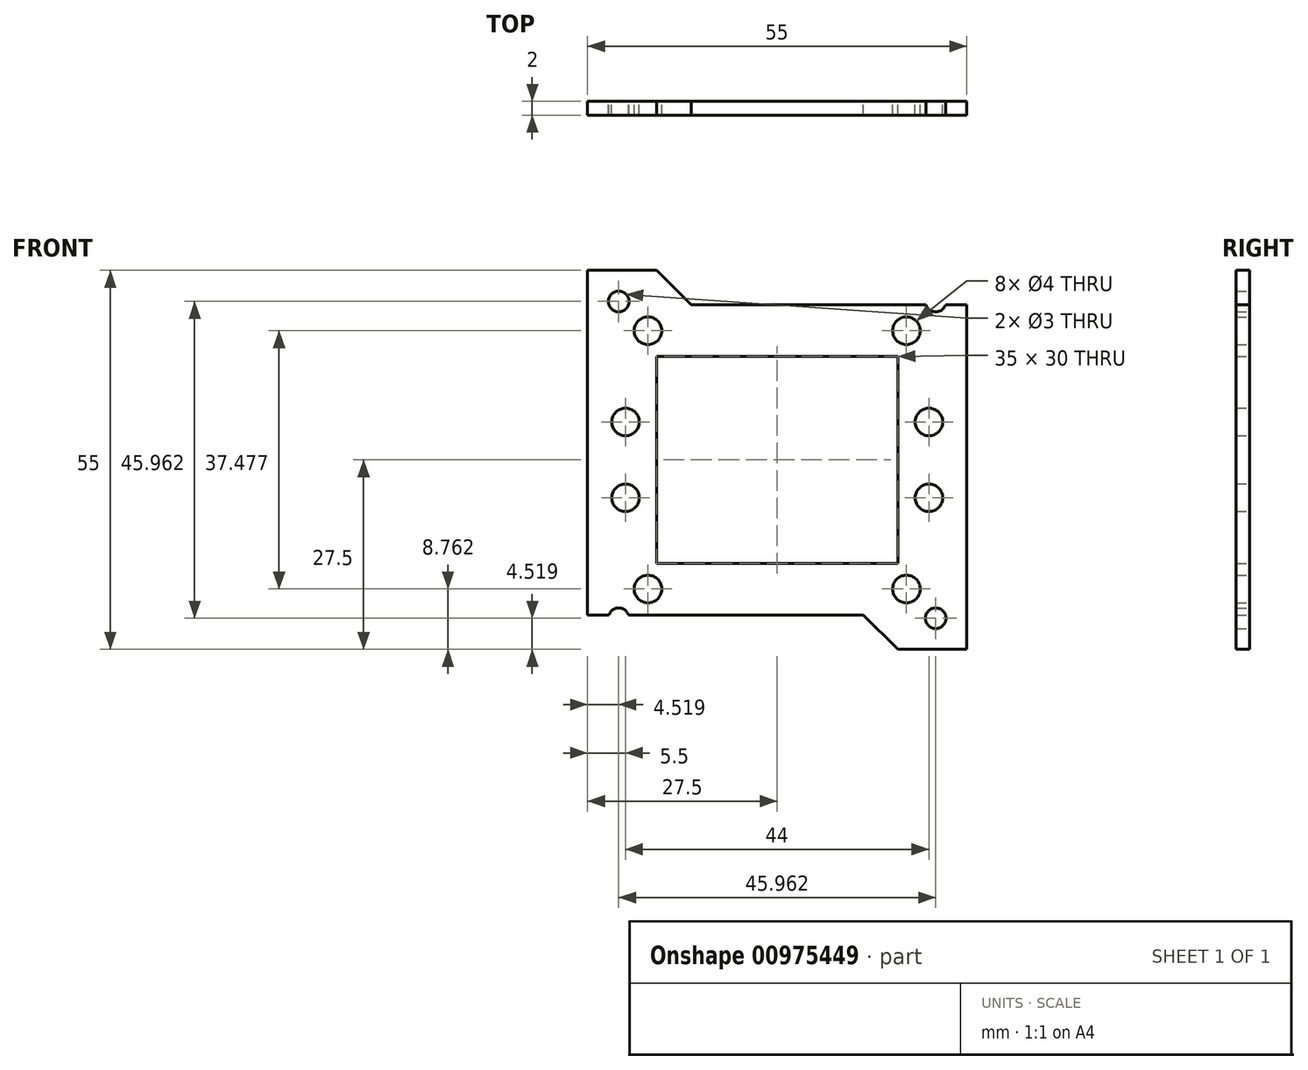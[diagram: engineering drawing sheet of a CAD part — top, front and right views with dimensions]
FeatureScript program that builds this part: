
annotation { "Feature Type Name" : "Feature", "Feature Type Description" : "" }
export const myFeature = defineFeature(function(context is Context, id is Id, definition is map)
    precondition{}
    {
        {
            var Q0;
            Q0=qCreatedBy(makeId("Front.planeOp"),FACE);
            var sketch = newSketch(context, id + "F0", { "sketchPlane" : qUnion([Q0])});
            skPoint(sketch, "E0.middle", {"position": v(0, 0) * mm});
            skCircle(sketch, "E1", {"center": v(-22.98, 22.98) * mm, "radius": 1.5 * mm});
            skCircle(sketch, "E2", {"center": v(22.98, -22.98) * mm, "radius": 1.5 * mm});
            skLineSegment(sketch, "E3.top", {"start": v(27.5, -27.5) * mm, "end": v(17.5, -27.5) * mm});
            skLineSegment(sketch, "E3.right", {"start": v(-27.5, 27.5) * mm, "end": v(-27.5, 17.5) * mm});
            skCircle(sketch, "E4", {"center": v(-18.74, 18.74) * mm, "radius": 2 * mm});
            skCircle(sketch, "E5.2.0", {"center": v(18.74, -18.74) * mm, "radius": 2 * mm});
            skLineSegment(sketch, "E6.trimOffspring", {"start": v(-17.5, 27.5) * mm, "end": v(-27.5, 27.5) * mm});
            skPoint(sketch, "E7.right.end.orphan", {"position": v(27.5, -17.5) * mm});
            skLineSegment(sketch, "E8.trimOffspring", {"start": v(27.5, -17.5) * mm, "end": v(27.5, -27.5) * mm});
            skLineSegment(sketch, "E9", {"start": v(-17.5, 27.5) * mm, "end": v(27.5, -17.5) * mm});
            skLineSegment(sketch, "E10", {"start": v(17.5, -27.5) * mm, "end": v(-27.5, 17.5) * mm});
            skLineSegment(sketch, "E11.bottom", {"start": v(27.5, 22.5) * mm, "end": v(-27.5, 22.5) * mm});
            skLineSegment(sketch, "E11.top", {"start": v(27.5, -22.5) * mm, "end": v(-27.5, -22.5) * mm});
            skLineSegment(sketch, "E11.left", {"start": v(27.5, 22.5) * mm, "end": v(27.5, -22.5) * mm});
            skLineSegment(sketch, "E11.right", {"start": v(-27.5, 22.5) * mm, "end": v(-27.5, -22.5) * mm});
            skCircle(sketch, "E12", {"center": v(22, 5.5) * mm, "radius": 2 * mm});
            skCircle(sketch, "E13", {"center": v(-22, -5.5) * mm, "radius": 2 * mm});
            skCircle(sketch, "E14", {"center": v(22, -5.5) * mm, "radius": 2 * mm});
            skCircle(sketch, "E15", {"center": v(-22, 5.5) * mm, "radius": 2 * mm});
            skLineSegment(sketch, "E16.bottom", {"start": v(17.5, 15) * mm, "end": v(-17.5, 15) * mm});
            skLineSegment(sketch, "E16.top", {"start": v(17.5, -15) * mm, "end": v(-17.5, -15) * mm});
            skLineSegment(sketch, "E16.left", {"start": v(17.5, 15) * mm, "end": v(17.5, -15) * mm});
            skLineSegment(sketch, "E16.right", {"start": v(-17.5, 15) * mm, "end": v(-17.5, -15) * mm});
            skCircle(sketch, "E17.1.0", {"center": v(18.74, 18.74) * mm, "radius": 2 * mm});
            skCircle(sketch, "E17.3.0", {"center": v(-18.74, -18.74) * mm, "radius": 2 * mm});
            skCircle(sketch, "E18.1.0", {"center": v(-22.98, -22.98) * mm, "radius": 1.5 * mm});
            skCircle(sketch, "E18.3.0", {"center": v(22.98, 22.98) * mm, "radius": 1.5 * mm});
            skSolve(sketch);
        }
        {
            var Q0;
            {var subQ5=sQuery(id+"F0.wireOp",EDGE,"E11.left");Q0=makeQuery(id+"F0.imprint","IMPRINT",FACE,{"disambiguationData":[TD([[makeQuery(id+"F0.imprint","IMPRINT",EDGE,{"derivedFrom":subQ5}),-1.0]])]});}
            var Q1;
            {var subQ0=sQuery(id+"F0.wireOp",EDGE,"E11.top");var subQ5=sQuery(id+"F0.wireOp",EDGE,"E5.2.0");var subQ13=makeQuery(id+"F0.imprint","INTERSECT",VERTEX,{"disambiguationData":[OD(0.0)],"derivedFrom":[subQ5,subQ0]});Q1=makeQuery(id+"F0.imprint","IMPRINT",FACE,{"disambiguationData":[TD([[makeQuery(id+"F0.imprint","IMPRINT",EDGE,{"disambiguationData":[TD([[subQ13,-1.0]])],"derivedFrom":subQ5}),-1.0]])]});}
            var Q2;
            Q2=makeQuery(id+"F0.imprint","IMPRINT",FACE,{"disambiguationData":[TD([[makeQuery(id+"F0.imprint","IMPRINT",EDGE,{"derivedFrom":sQuery(id+"F0.wireOp",EDGE,"E2")}),-1.0]])]});
            var Q3;
            {var subQ7=sQuery(id+"F0.wireOp",EDGE,"E11.right");Q3=makeQuery(id+"F0.imprint","IMPRINT",FACE,{"disambiguationData":[TD([[makeQuery(id+"F0.imprint","IMPRINT",EDGE,{"derivedFrom":subQ7}),1.0]])]});}
            var Q4;
            {var subQ8=sQuery(id+"F0.wireOp",EDGE,"E10");var subQ9=sQuery(id+"F0.wireOp",EDGE,"E3.right");var subQ10=makeQuery(id+"F0.imprint","INTERSECT",VERTEX,{"derivedFrom":[subQ9,subQ8]});Q4=makeQuery(id+"F0.imprint","IMPRINT",FACE,{"disambiguationData":[TD([[makeQuery(id+"F0.imprint","IMPRINT",EDGE,{"disambiguationData":[TD([[subQ10,1.0]])],"derivedFrom":subQ9}),1.0]])]});}
            var Q5;
            Q5=makeQuery(id+"F0.imprint","IMPRINT",FACE,{"disambiguationData":[TD([[makeQuery(id+"F0.imprint","IMPRINT",EDGE,{"derivedFrom":sQuery(id+"F0.wireOp",EDGE,"E1")}),-1.0]])]});
            var Q6;
            Q6=makeQuery(id+"F0.imprint","IMPRINT",FACE,{"disambiguationData":[TD([[makeQuery(id+"F0.imprint","IMPRINT",EDGE,{"derivedFrom":sQuery(id+"F0.wireOp",EDGE,"E13")}),-1.0]])]});
            var Q7;
            Q7=makeQuery(id+"F0.imprint","IMPRINT",FACE,{"disambiguationData":[TD([[makeQuery(id+"F0.imprint","IMPRINT",EDGE,{"derivedFrom":sQuery(id+"F0.wireOp",EDGE,"E12")}),-1.0]])]});
            var Q8;
            {var subQ5=sQuery(id+"F0.wireOp",EDGE,"E3.top");Q8=makeQuery(id+"F0.imprint","IMPRINT",FACE,{"disambiguationData":[TD([[makeQuery(id+"F0.imprint","IMPRINT",EDGE,{"derivedFrom":subQ5}),-1.0]])]});}
            extrude(context, id + "F1", {"entities" : qUnion([Q0, Q1, Q2, Q3, Q4, Q5, Q6, Q7, Q8]), "depth" : 2 * mm, "offsetDistance" : 25 * mm});
        }
    });
